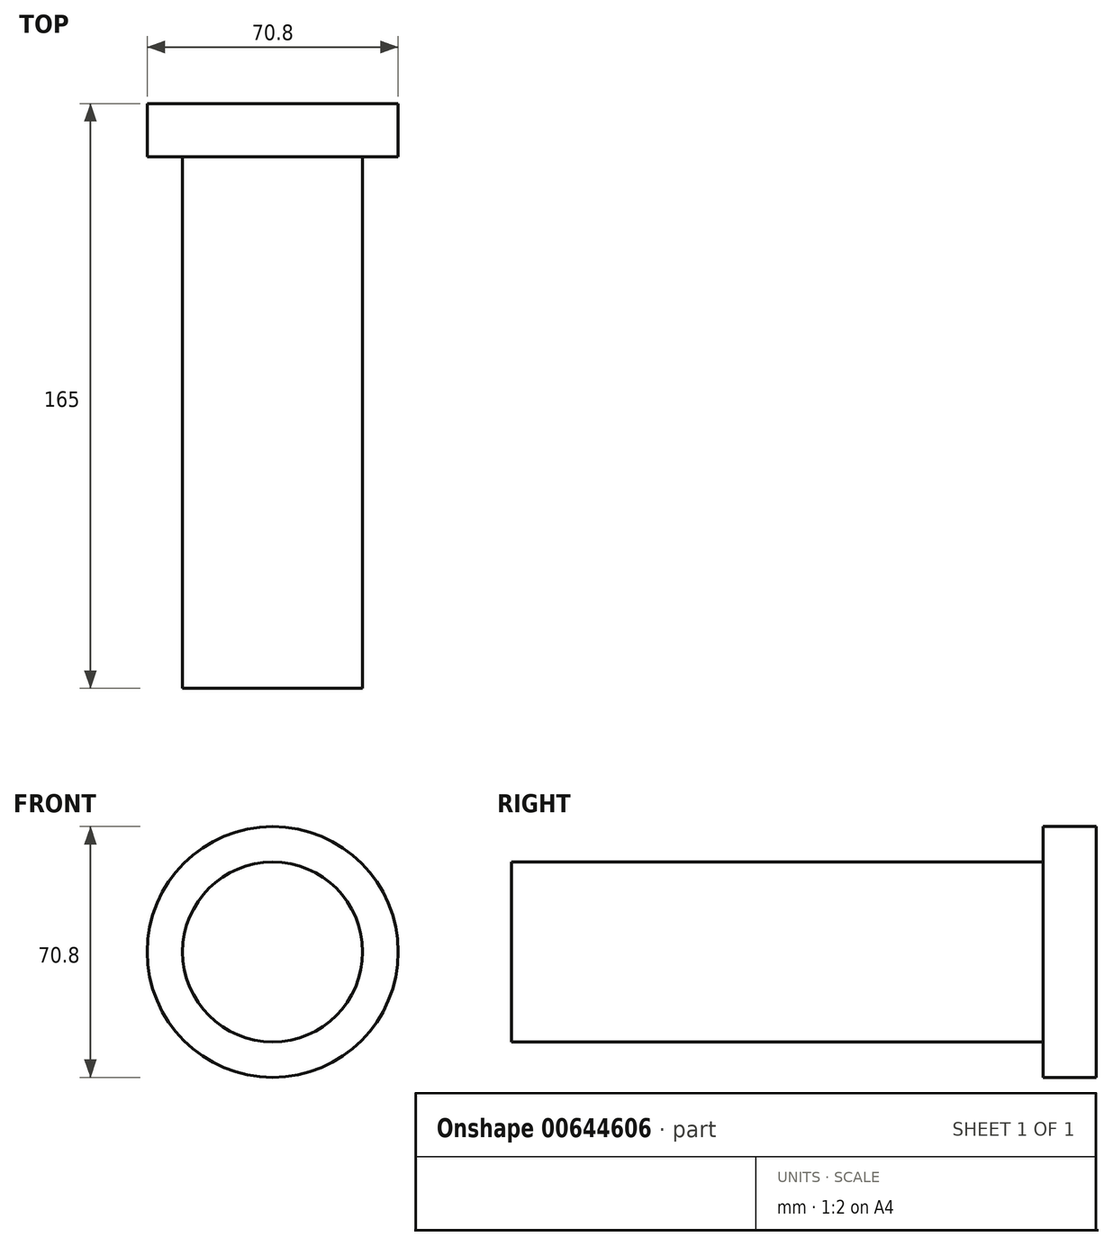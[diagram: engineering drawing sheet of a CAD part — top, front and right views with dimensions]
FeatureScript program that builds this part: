
annotation { "Feature Type Name" : "Feature", "Feature Type Description" : "" }
export const myFeature = defineFeature(function(context is Context, id is Id, definition is map)
    precondition{}
    {
        {
            var Q0;
            Q0=qCreatedBy(makeId("Front.planeOp"),FACE);
            var sketch = newSketch(context, id + "F0", { "sketchPlane" : qUnion([Q0])});
            skCircle(sketch, "E0", {"center": v(0, 0) * mm, "radius": 25.4 * mm});
            skSolve(sketch);
        }
        {
            var Q0;
            Q0=makeQuery(id+"F0.imprint","IMPRINT",FACE,{"disambiguationData":[TD([[makeQuery(id+"F0.imprint","IMPRINT",EDGE,{"derivedFrom":sQuery(id+"F0.wireOp",EDGE,"E0")}),1.0]])]});
            extrude(context, id + "F1", {"entities" : qUnion([Q0]), "depth" : 150 * mm, "offsetDistance" : 25 * mm});
        }
        {
            var Q0;
            Q0=qCreatedBy(makeId("Front.planeOp"),FACE);
            var sketch = newSketch(context, id + "F2", { "sketchPlane" : qUnion([Q0])});
            skCircle(sketch, "E1", {"center": v(0, 0) * mm, "radius": 35.4 * mm});
            skSolve(sketch);
        }
        {
            var Q0;
            Q0 = qSketchRegion(id + "F2", true);
            extrude(context, id + "F3", {"entities" : qUnion([Q0]), "operationType" : NewBodyOperationType.ADD, "oppositeDirection" : true, "depth" : 15 * mm, "offsetDistance" : 25 * mm});
        }
    });
